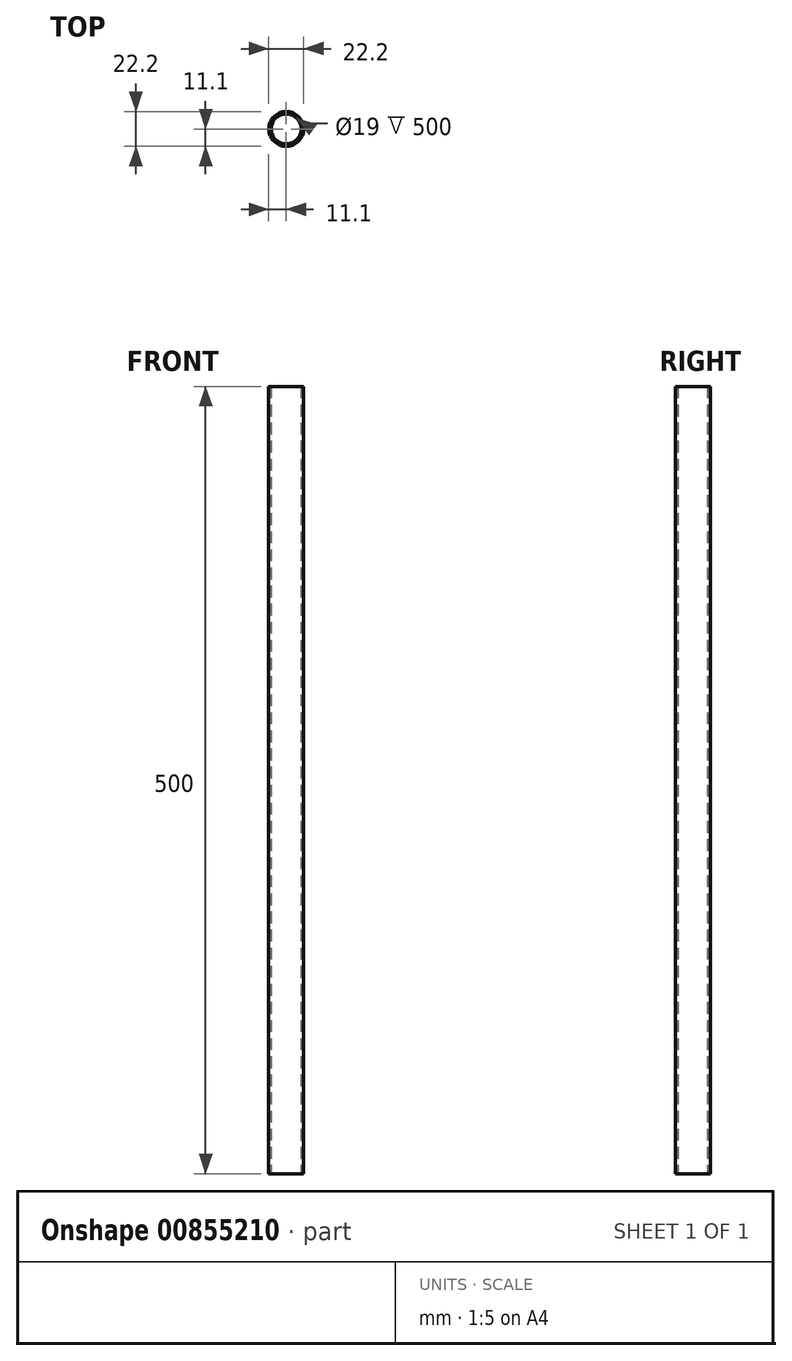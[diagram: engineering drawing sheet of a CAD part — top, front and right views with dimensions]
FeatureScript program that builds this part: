
annotation { "Feature Type Name" : "Feature", "Feature Type Description" : "" }
export const myFeature = defineFeature(function(context is Context, id is Id, definition is map)
    precondition{}
    {
        {
            var Q0;
            Q0=qCreatedBy(makeId("Top.planeOp"),FACE);
            var sketch = newSketch(context, id + "F0", { "sketchPlane" : qUnion([Q0])});
            skCircle(sketch, "E0", {"center": v(0, 0) * mm, "radius": 11.1 * mm});
            skCircle(sketch, "E1", {"center": v(0, 0) * mm, "radius": 9.5 * mm});
            skSolve(sketch);
        }
        {
            var Q0;
            Q0 = qSketchRegion(id + "F0", true);
            extrude(context, id + "F1", {"entities" : qUnion([Q0]), "depth" : 500 * mm, "offsetDistance" : 25 * mm});
        }
    });
